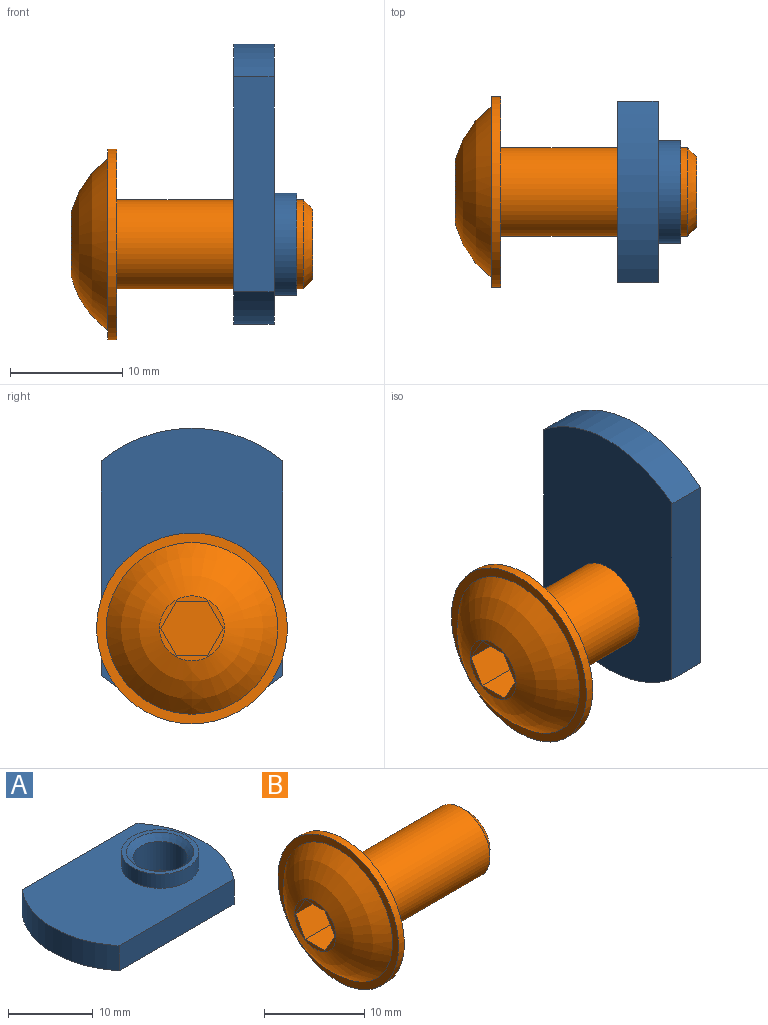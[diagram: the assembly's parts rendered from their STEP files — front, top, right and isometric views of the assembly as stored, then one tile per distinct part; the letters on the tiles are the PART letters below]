
ASSEMBLY  parts=2 mates=1
PART A: 11 faces, bbox 25x16.2x5.6 mm
  f0: plane 19.17x3.61mm, normal (0,1,0), area 69.2mm2, adj f1,f3,f4,f5
  f1: cylinder r=12.7mm len=16.18mm, axis (0,0,-1), area 63.3mm2, adj f0,f2,f4,f5
  f2: plane 19.17x3.61mm, normal (0,-1,0), area 69.2mm2, adj f1,f3,f4,f5
  f3: cylinder r=12.7mm len=16.18mm, axis (0,0,-1), area 63.3mm2, adj f0,f2,f4,f5
  f4: plane 24.99x16.18mm, normal (0,0,1), area 309.3mm2, adj f0,f1,f2,f3,f6
  f5: plane 24.99x16.18mm, normal (0,0,-1), area 325.1mm2, adj f0,f1,f2,f3,f10
  f6: cylinder r=4.56mm len=9.12mm, axis (0,0,-1), area 58.2mm2, adj f4,f7
  f7: plane 9.12x9.12mm, normal (0,0,1), area 15.8mm2, adj f6,f8
  f8: cone r=3.97mm half-angle=45deg, axis (0,0,1), area 24.3mm2, adj f7,f9
  f9: cylinder r=3.21mm len=6.41mm, axis (0,0,-1), area 82.8mm2, adj f8,f10
  f10: cone r=3.21mm half-angle=45deg, axis (0,0,-1), area 24.3mm2, adj f5,f9
PART B: 15 faces, bbox 21.5x17x17 mm
  f0: plane 5.79x5.79mm, normal (-1,0,0), area 6.2mm2, adj f1,f8,f9,f10,f11,f12,f13
  f1: torus R=0.76mm, axis (1,0,0), area 202mm2, adj f0,f2
  f2: plane 17.02x17.02mm, normal (-1,0,0), area 43.2mm2, adj f1,f3
  f3: cylinder r=8.51mm len=17.02mm, axis (1,0,0), area 43.5mm2, adj f2,f4
  f4: plane 17.02x17.02mm, normal (1,0,0), area 178mm2, adj f3,f5
  f5: cylinder r=3.97mm len=16.62mm, axis (1,0,0), area 414.5mm2, adj f4,f6
  f6: cone r=3.97mm half-angle=45deg, axis (-1,0,0), area 26.5mm2, adj f5,f7
  f7: plane 6.26x6.26mm, normal (1,0,0), area 30.8mm2, adj f6
  f8: plane 3.56x2.79mm, normal (0,0,-1), area 9.9mm2, adj f0,f9,f13,f14
  f9: plane 3.56x2.41mm, normal (0,0.87,-0.5), area 9.9mm2, adj f0,f8,f10,f14
  f10: plane 3.56x2.41mm, normal (0,0.87,0.5), area 9.9mm2, adj f0,f9,f11,f14
  f11: plane 3.56x2.79mm, normal (0,0,1), area 9.9mm2, adj f0,f10,f12,f14
  f12: plane 3.56x2.41mm, normal (0,-0.87,0.5), area 9.9mm2, adj f0,f11,f13,f14
  f13: plane 3.56x2.41mm, normal (0,-0.87,-0.5), area 9.9mm2, adj f0,f8,f12,f14
  f14: plane 5.57x4.83mm, normal (-1,0,0), area 20.2mm2, adj f8,f9,f10,f11,f12,f13
PLACE A rot(axis=(0,1,0),90deg) t=(12.22,0,0)mm
PLACE B at identity fixed
MATE fastened A.f6 <-> B.f1  axis (-1,0,0) through (10.41,0,0)mm
